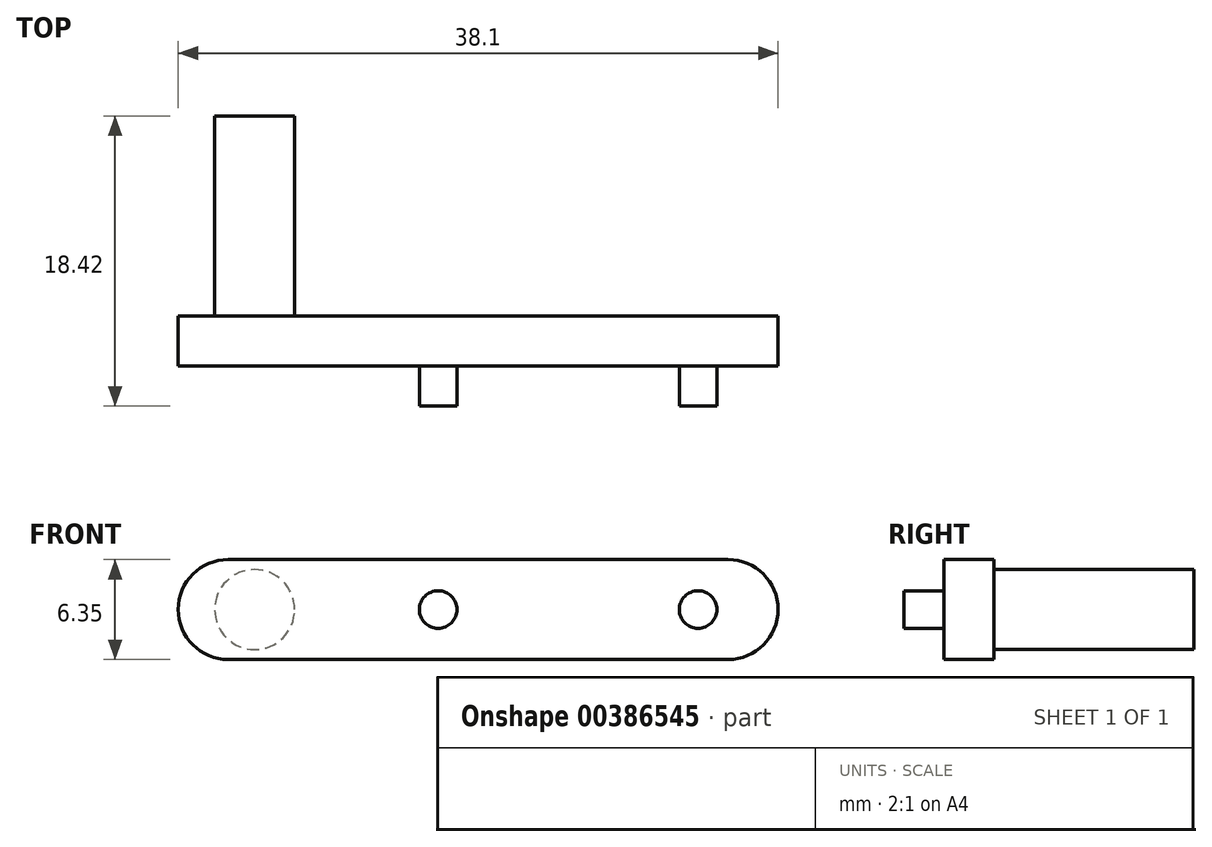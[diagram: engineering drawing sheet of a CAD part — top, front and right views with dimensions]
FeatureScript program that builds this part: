
annotation { "Feature Type Name" : "Feature", "Feature Type Description" : "" }
export const myFeature = defineFeature(function(context is Context, id is Id, definition is map)
    precondition{}
    {
        {
            var Q0;
            Q0=qCreatedBy(makeId("Front.planeOp"),FACE);
            var sketch = newSketch(context, id + "F0", { "sketchPlane" : qUnion([Q0])});
            skLineSegment(sketch, "E0.bottom", {"start": v(-25.15, 4.9) * mm, "end": v(12.95, 4.9) * mm});
            skLineSegment(sketch, "E0.top", {"start": v(-25.15, -1.44) * mm, "end": v(12.95, -1.44) * mm});
            skLineSegment(sketch, "E0.left", {"start": v(-25.15, 4.9) * mm, "end": v(-25.15, -1.44) * mm});
            skLineSegment(sketch, "E0.right", {"start": v(12.95, 4.9) * mm, "end": v(12.95, -1.44) * mm});
            skSolve(sketch);
        }
        {
            var Q0;
            Q0 = qSketchRegion(id + "F0", true);
            extrude(context, id + "F1", {"entities" : qUnion([Q0]), "depth" : 3.17 * mm});
        }
        {
            var Q0;
            Q0=makeQuery(id+"F1.opExtrude","SWEPT_EDGE",EDGE,{"disambiguationData":[OSD([sQuery(id+"F0.wireOp",EDGE,"E0.top"),sQuery(id+"F0.wireOp",EDGE,"E0.left")])]});
            var Q1;
            Q1=makeQuery(id+"F1.opExtrude","SWEPT_EDGE",EDGE,{"disambiguationData":[OSD([sQuery(id+"F0.wireOp",EDGE,"E0.bottom"),sQuery(id+"F0.wireOp",EDGE,"E0.left")])]});
            var Q2;
            Q2=makeQuery(id+"F1.opExtrude","SWEPT_EDGE",EDGE,{"disambiguationData":[OSD([sQuery(id+"F0.wireOp",EDGE,"E0.bottom"),sQuery(id+"F0.wireOp",EDGE,"E0.right")])]});
            var Q3;
            Q3=makeQuery(id+"F1.opExtrude","SWEPT_EDGE",EDGE,{"disambiguationData":[OSD([sQuery(id+"F0.wireOp",EDGE,"E0.top"),sQuery(id+"F0.wireOp",EDGE,"E0.right")])]});
            fillet(context, id + "F2", {"entities" : qUnion([Q0, Q1, Q2, Q3]), "radius" : 3.17 * mm, "tangentPropagation" : true, "allowEdgeOverflow" : false});
        }
        {
            var Q0;
            Q0=makeQuery(id+"F1.opExtrude","CAP_FACE",FACE,{"disambiguationData":[OSD([sQuery(id+"F0.wireOp",EDGE,"E0.bottom"),sQuery(id+"F0.wireOp",EDGE,"E0.top"),sQuery(id+"F0.wireOp",EDGE,"E0.left"),sQuery(id+"F0.wireOp",EDGE,"E0.right")])],"isStart":false});
            var sketch = newSketch(context, id + "F3", { "sketchPlane" : qUnion([Q0])});
            skPoint(sketch, "E1", {"position": v(-20.3, 1.73) * mm});
            skPoint(sketch, "E2", {"position": v(-8.64, 1.73) * mm});
            skPoint(sketch, "E3", {"position": v(7.87, 1.73) * mm});
            skCircle(sketch, "E4", {"center": v(-20.3, 1.73) * mm, "radius": 2.54 * mm});
            skCircle(sketch, "E5", {"center": v(-8.64, 1.73) * mm, "radius": 1.2 * mm});
            skCircle(sketch, "E6", {"center": v(7.87, 1.73) * mm, "radius": 1.2 * mm});
            skSolve(sketch);
        }
        {
            var Q0;
            Q0=makeQuery(id+"F3.imprint","IMPRINT",FACE,{"disambiguationData":[TD([[makeQuery(id+"F3.imprint","IMPRINT",EDGE,{"derivedFrom":sQuery(id+"F3.wireOp",EDGE,"E5")}),1.0]])]});
            var Q1;
            Q1=makeQuery(id+"F3.imprint","IMPRINT",FACE,{"disambiguationData":[TD([[makeQuery(id+"F3.imprint","IMPRINT",EDGE,{"derivedFrom":sQuery(id+"F3.wireOp",EDGE,"E6")}),1.0]])]});
            extrude(context, id + "F4", {"entities" : qUnion([Q0, Q1]), "operationType" : NewBodyOperationType.ADD, "depth" : 2.54 * mm});
        }
        {
            var Q0;
            Q0=makeQuery(id+"F1.opExtrude","CAP_FACE",FACE,{"disambiguationData":[OSD([sQuery(id+"F0.wireOp",EDGE,"E0.bottom"),sQuery(id+"F0.wireOp",EDGE,"E0.top"),sQuery(id+"F0.wireOp",EDGE,"E0.left"),sQuery(id+"F0.wireOp",EDGE,"E0.right")])],"isStart":true});
            var sketch = newSketch(context, id + "F5", { "sketchPlane" : qUnion([Q0])});
            skPoint(sketch, "E7.positionSnap0", {"position": v(25.15, 1.73) * mm});
            skPoint(sketch, "E8", {"position": v(20.3, 1.73) * mm});
            skCircle(sketch, "E9", {"center": v(20.3, 1.73) * mm, "radius": 2.54 * mm});
            skSolve(sketch);
        }
        {
            var Q0;
            Q0 = qSketchRegion(id + "F5", true);
            extrude(context, id + "F6", {"entities" : qUnion([Q0]), "operationType" : NewBodyOperationType.ADD, "depth" : 12.7 * mm});
        }
    });
